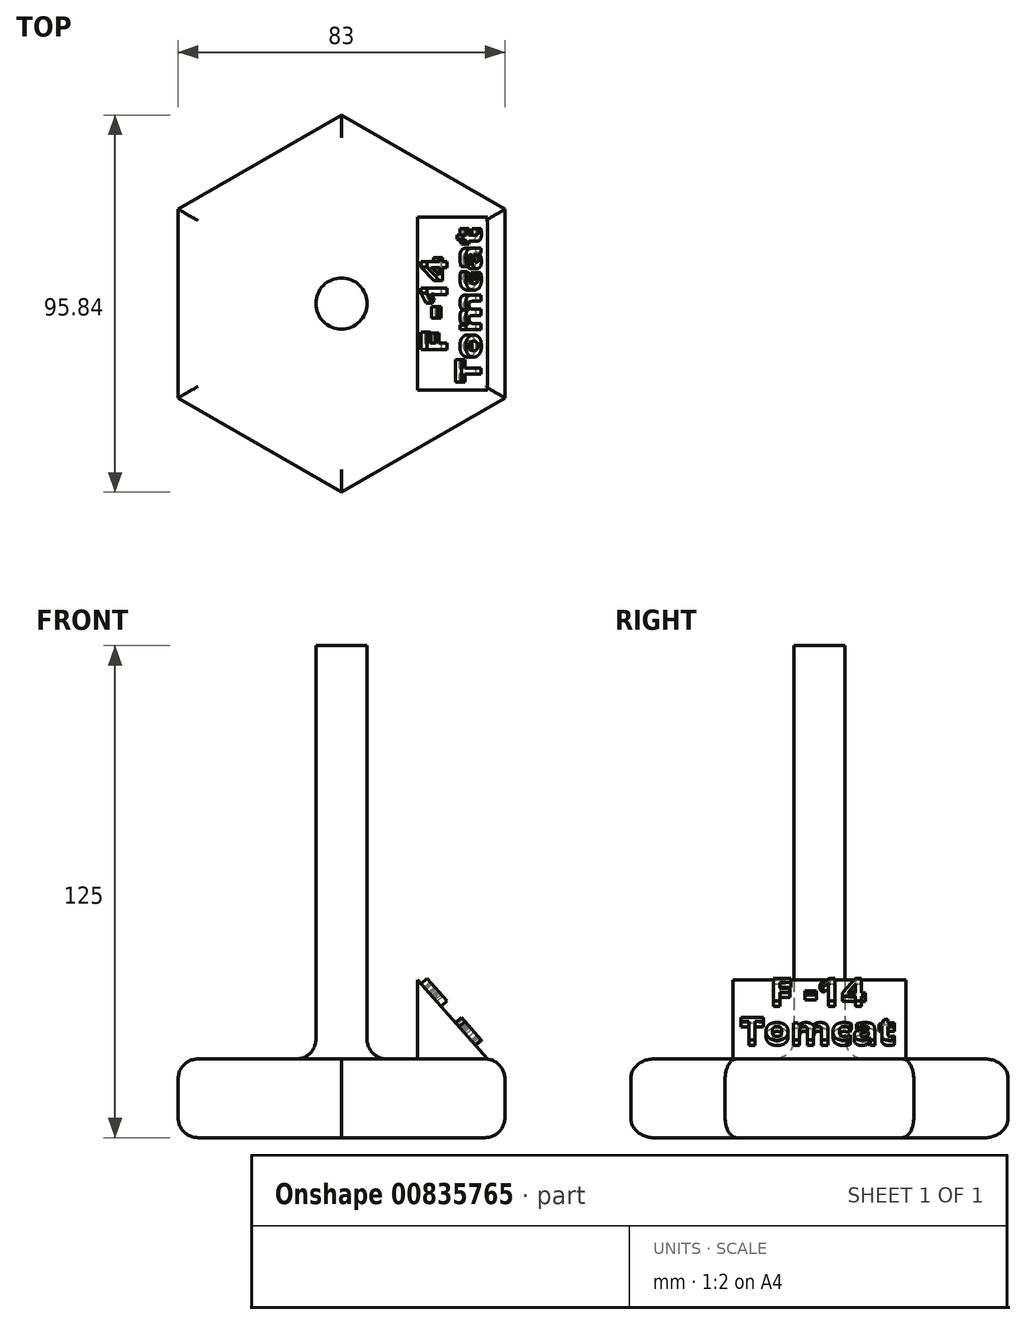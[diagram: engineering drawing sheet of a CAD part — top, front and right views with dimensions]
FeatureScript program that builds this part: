
annotation { "Feature Type Name" : "Feature", "Feature Type Description" : "" }
export const myFeature = defineFeature(function(context is Context, id is Id, definition is map)
    precondition{}
    {
        {
            var Q0;
            Q0=qCreatedBy(makeId("Top.planeOp"),FACE);
            var sketch = newSketch(context, id + "F0", { "sketchPlane" : qUnion([Q0])});
            skCircle(sketch, "E0.cCircle", {"center": v(0, 0) * mm, "radius": 41.5 * mm, "construction": true});
            skLineSegment(sketch, "E0.0", {"start": v(41.5, 23.96) * mm, "end": v(41.5, -23.96) * mm});
            skLineSegment(sketch, "E0.1", {"start": v(41.5, -23.96) * mm, "end": v(0, -47.92) * mm});
            skLineSegment(sketch, "E0.2", {"start": v(0, -47.92) * mm, "end": v(-41.5, -23.96) * mm});
            skLineSegment(sketch, "E0.3", {"start": v(-41.5, -23.96) * mm, "end": v(-41.5, 23.96) * mm});
            skLineSegment(sketch, "E0.4", {"start": v(-41.5, 23.96) * mm, "end": v(0, 47.92) * mm});
            skLineSegment(sketch, "E0.5", {"start": v(0, 47.92) * mm, "end": v(41.5, 23.96) * mm});
            skPoint(sketch, "E0.0.midPoint", {"position": v(41.5, 0) * mm});
            skCircle(sketch, "E1", {"center": v(0, 0) * mm, "radius": 6.5 * mm});
            skSolve(sketch);
        }
        {
            var Q0;
            Q0 = qSketchRegion(id + "F0", true);
            extrude(context, id + "F1", {"entities" : qUnion([Q0]), "depth" : 20 * mm, "offsetDistance" : 25 * mm});
        }
        {
            var Q0;
            Q0=makeQuery(id+"F0.imprint","IMPRINT",FACE,{"disambiguationData":[TD([[makeQuery(id+"F0.imprint","IMPRINT",EDGE,{"derivedFrom":sQuery(id+"F0.wireOp",EDGE,"E1")}),1.0]])]});
            extrude(context, id + "F2", {"entities" : qUnion([Q0]), "operationType" : NewBodyOperationType.ADD, "depth" : 125 * mm, "offsetDistance" : 25 * mm});
        }
        {
            var Q0;
            Q0=makeQuery(id+"F1.opExtrude","CAP_FACE",FACE,{"disambiguationData":[OSD([sQuery(id+"F0.wireOp",EDGE,"E0.0"),sQuery(id+"F0.wireOp",EDGE,"E0.1"),sQuery(id+"F0.wireOp",EDGE,"E0.2"),sQuery(id+"F0.wireOp",EDGE,"E0.3"),sQuery(id+"F0.wireOp",EDGE,"E0.4"),sQuery(id+"F0.wireOp",EDGE,"E0.5"),sQuery(id+"F0.wireOp",EDGE,"E1")])],"isStart":false});
            var Q1;
            Q1=makeQuery(id+"F1.opExtrude","CAP_EDGE",EDGE,{"disambiguationData":[OSD([sQuery(id+"F0.wireOp",EDGE,"E0.4")])],"isStart":true});
            var Q2;
            Q2=makeQuery(id+"F1.opExtrude","CAP_EDGE",EDGE,{"disambiguationData":[OSD([sQuery(id+"F0.wireOp",EDGE,"E0.3")])],"isStart":true});
            var Q3;
            {var subQ0=sQuery(id+"F0.wireOp",EDGE,"E1");Q3=makeQuery(id+"F2.boolean.opBoolean","MERGE",FACE,{"derivedFrom":[makeQuery(id+"F1.opExtrude","CAP_FACE",FACE,{"disambiguationData":[OSD([sQuery(id+"F0.wireOp",EDGE,"E0.0"),sQuery(id+"F0.wireOp",EDGE,"E0.1"),sQuery(id+"F0.wireOp",EDGE,"E0.2"),sQuery(id+"F0.wireOp",EDGE,"E0.3"),sQuery(id+"F0.wireOp",EDGE,"E0.4"),sQuery(id+"F0.wireOp",EDGE,"E0.5"),subQ0])],"isStart":true}),makeQuery(id+"F2.opExtrude","CAP_FACE",FACE,{"disambiguationData":[OSD([subQ0])],"isStart":true})]});}
            var Q4;
            Q4=makeQuery(id+"F1.opExtrude","CAP_EDGE",EDGE,{"disambiguationData":[OSD([sQuery(id+"F0.wireOp",EDGE,"E1")])],"isStart":false});
            fillet(context, id + "F3", {"entities" : qUnion([Q0, Q1, Q2, Q3, Q4]), "radius" : 5 * mm, "tangentPropagation" : true, "allowEdgeOverflow" : false});
        }
        {
            var Q0;
            Q0=qCreatedBy(makeId("Front.planeOp"),FACE);
            var sketch = newSketch(context, id + "F4", { "sketchPlane" : qUnion([Q0])});
            skLineSegment(sketch, "E2", {"start": v(19.33, 20.05) * mm, "end": v(19.33, 40.09) * mm});
            skLineSegment(sketch, "E3", {"start": v(19.33, 40.09) * mm, "end": v(37.04, 20.05) * mm});
            skLineSegment(sketch, "E4", {"start": v(37.04, 20.05) * mm, "end": v(19.33, 20.05) * mm});
            skSolve(sketch);
        }
        {
            var Q0;
            Q0=makeQuery(id+"F4.imprint","IMPRINT",FACE,{"disambiguationData":[TD([[makeQuery(id+"F4.imprint","IMPRINT",EDGE,{"derivedFrom":sQuery(id+"F4.wireOp",EDGE,"E2")}),-1.0]])]});
            extrude(context, id + "F5", {"entities" : qUnion([Q0]), "endBound" : BoundingType.SYMMETRIC, "depth" : 44 * mm, "offsetDistance" : 25 * mm});
        }
        {
            var Q0;
            Q0=makeQuery(id+"F5.opExtrude","SWEPT_FACE",FACE,{"disambiguationData":[OSD([sQuery(id+"F4.wireOp",EDGE,"E3")])]});
            var sketch = newSketch(context, id + "F6", { "sketchPlane" : qUnion([Q0])});
            skText(sketch, "E5", { "text": "F -14 ", "fontName": "OpenSans-Bold.ttf"});
            const initialGuessF6  = {"E5": [-0.01266, 0.00827, 1, 0, 0.00775]};
            skSetInitialGuess(sketch, initialGuessF6);
            skSolve(sketch);
        }
        {
            var Q0;
            Q0 = qSketchRegion(id + "F6", true);
            extrude(context, id + "F7", {"entities" : qUnion([Q0]), "operationType" : NewBodyOperationType.ADD, "depth" : 2 * mm, "offsetDistance" : 25 * mm});
        }
        {
            var Q0;
            {var subQ1=sQuery(id+"F4.wireOp",EDGE,"E3");var subQ2=sQuery(id+"F4.wireOp",EDGE,"E2");Q0=makeQuery(id+"F7.boolean.opBoolean","SPLIT",FACE,{"disambiguationData":[TD([makeQuery(id+"F5.opExtrude","SWEPT_FACE",FACE,{"disambiguationData":[OSD([subQ2])]})])],"derivedFrom":makeQuery(id+"F5.opExtrude","SWEPT_FACE",FACE,{"disambiguationData":[OSD([subQ1])]})});}
            var sketch = newSketch(context, id + "F8", { "sketchPlane" : qUnion([Q0])});
            skText(sketch, "E6", { "text": "Tomcat", "fontName": "OpenSans-Bold.ttf"});
            const initialGuessF8  = {"E6": [-0.02021, -0.00489, 1, 0, 0.00765]};
            skSetInitialGuess(sketch, initialGuessF8);
            skSolve(sketch);
        }
        {
            var Q0;
            Q0=makeQuery(id+"F8.imprint","IMPRINT",FACE,{"disambiguationData":[TD([[makeQuery(id+"F8.imprint","IMPRINT",EDGE,{"derivedFrom":sQuery(id+"F8.wireOp",EDGE,"E6.sketch_text.stroke-0")}),-1.0]])]});
            var Q1;
            Q1=makeQuery(id+"F8.imprint","IMPRINT",FACE,{"disambiguationData":[TD([[makeQuery(id+"F8.imprint","IMPRINT",EDGE,{"derivedFrom":sQuery(id+"F8.wireOp",EDGE,"E6.sketch_text.stroke-8")}),-1.0]])]});
            var Q2;
            Q2=makeQuery(id+"F8.imprint","IMPRINT",FACE,{"disambiguationData":[TD([[makeQuery(id+"F8.imprint","IMPRINT",EDGE,{"derivedFrom":sQuery(id+"F8.wireOp",EDGE,"E6.sketch_text.stroke-26")}),-1.0]])]});
            var Q3;
            Q3=makeQuery(id+"F8.imprint","IMPRINT",FACE,{"disambiguationData":[TD([[makeQuery(id+"F8.imprint","IMPRINT",EDGE,{"derivedFrom":sQuery(id+"F8.wireOp",EDGE,"E6.sketch_text.stroke-54")}),-1.0]])]});
            var Q4;
            Q4=makeQuery(id+"F8.imprint","IMPRINT",FACE,{"disambiguationData":[TD([[makeQuery(id+"F8.imprint","IMPRINT",EDGE,{"derivedFrom":sQuery(id+"F8.wireOp",EDGE,"E6.sketch_text.stroke-68")}),-1.0]])]});
            var Q5;
            Q5=makeQuery(id+"F8.imprint","IMPRINT",FACE,{"disambiguationData":[TD([[makeQuery(id+"F8.imprint","IMPRINT",EDGE,{"derivedFrom":sQuery(id+"F8.wireOp",EDGE,"E6.sketch_text.stroke-93")}),-1.0]])]});
            extrude(context, id + "F9", {"entities" : qUnion([Q0, Q1, Q2, Q3, Q4, Q5]), "operationType" : NewBodyOperationType.ADD, "depth" : 2 * mm, "offsetDistance" : 25 * mm});
        }
    });
